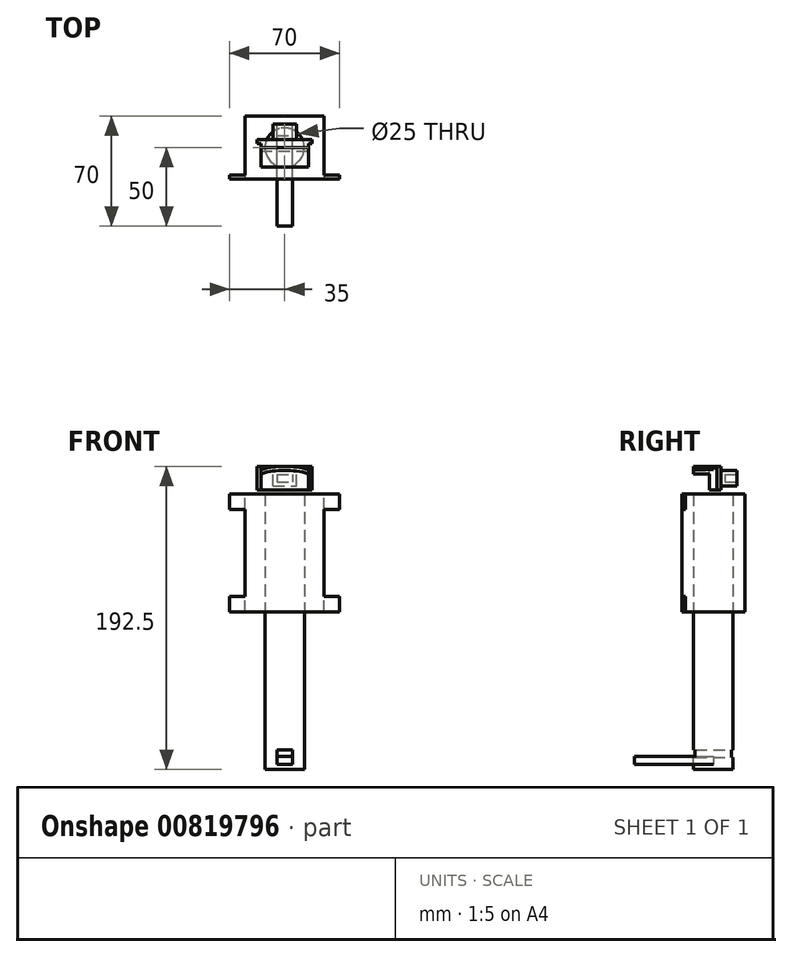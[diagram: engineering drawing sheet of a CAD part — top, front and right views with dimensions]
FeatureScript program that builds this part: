
annotation { "Feature Type Name" : "Feature", "Feature Type Description" : "" }
export const myFeature = defineFeature(function(context is Context, id is Id, definition is map)
    precondition{}
    {
        {
            var Q0;
            Q0=qCreatedBy(makeId("Front.planeOp"),FACE);
            var sketch = newSketch(context, id + "F0", { "sketchPlane" : qUnion([Q0])});
            skCircle(sketch, "E0", {"center": v(0, 0) * mm, "radius": 55 * mm});
            skSolve(sketch);
        }
        {
            var Q0;
            Q0=makeQuery(id+"F0.imprint","IMPRINT",FACE,{"disambiguationData":[TD([[makeQuery(id+"F0.imprint","IMPRINT",EDGE,{"derivedFrom":sQuery(id+"F0.wireOp",EDGE,"E0")}),1.0]])]});
            extrude(context, id + "F1", {"entities" : qUnion([Q0]), "depth" : 12.5 * mm, "offsetDistance" : 25 * mm});
        }
        {
            var Q0;
            Q0=makeQuery(id+"F1.opExtrude","CAP_FACE",FACE,{"disambiguationData":[OSD([sQuery(id+"F0.wireOp",EDGE,"E0")])],"isStart":false});
            shell(context, id + "F2", {"entities" : qUnion([Q0]), "thickness" : 2.5 * mm});
        }
        {
            var Q0;
            Q0=makeQuery(id+"F1.opExtrude","CAP_FACE",FACE,{"disambiguationData":[OSD([sQuery(id+"F0.wireOp",EDGE,"E0")])],"isStart":false});
            var sketch = newSketch(context, id + "F3", { "sketchPlane" : qUnion([Q0])});
            skLineSegment(sketch, "E1.bottom", {"start": v(-55, 55) * mm, "end": v(55, 55) * mm});
            skLineSegment(sketch, "E1.top", {"start": v(-55, -55) * mm, "end": v(55, -55) * mm});
            skLineSegment(sketch, "E1.left", {"start": v(-55, 55) * mm, "end": v(-55, -55) * mm});
            skLineSegment(sketch, "E1.right", {"start": v(55, 55) * mm, "end": v(55, -55) * mm});
            skPoint(sketch, "E1.middle", {"position": v(0, 0) * mm});
            skLineSegment(sketch, "E2.bottom", {"start": v(15, 55) * mm, "end": v(-15, 55) * mm});
            skLineSegment(sketch, "E2.top", {"start": v(15, 40) * mm, "end": v(-15, 40) * mm});
            skLineSegment(sketch, "E2.left", {"start": v(15, 55) * mm, "end": v(15, 40) * mm});
            skLineSegment(sketch, "E2.right", {"start": v(-15, 55) * mm, "end": v(-15, 40) * mm});
            skPoint(sketch, "E2.middle", {"position": v(0, 47.5) * mm});
            skPoint(sketch, "E2.middle.positionSnap0", {"position": v(0, 55) * mm});
            skPoint(sketch, "E2.centerSnap0", {"position": v(0, 55) * mm});
            skSolve(sketch);
        }
        {
            var Q0;
            {var subQ0=sQuery(id+"F3.wireOp",EDGE,"E2.top");Q0=makeQuery(id+"F3.imprint","IMPRINT",FACE,{"disambiguationData":[TD([[makeQuery(id+"F3.imprint","IMPRINT",EDGE,{"derivedFrom":subQ0}),1.0]])]});}
            var Q1;
            {var subQ0=sQuery(id+"F0.wireOp",EDGE,"E0");var subQ1=makeQuery(id+"F1.opExtrude","CAP_EDGE",EDGE,{"disambiguationData":[OSD([subQ0])],"isStart":false});var subQ2=makeQuery(id+"F3.imprint","INTERSECT",VERTEX,{"derivedFrom":[subQ1,sQuery(id+"F3.wireOp",EDGE,"E1.top")]});Q1=makeQuery(id+"F3.imprint","IMPRINT",FACE,{"disambiguationData":[TD([[makeQuery(id+"F3.imprint","IMPRINT",EDGE,{"disambiguationData":[TD([[subQ2,1.0]])],"derivedFrom":subQ1}),1.0]])]});}
            extrude(context, id + "F4", {"entities" : qUnion([Q0, Q1]), "operationType" : NewBodyOperationType.REMOVE, "oppositeDirection" : true, "depth" : 25 * mm, "offsetDistance" : 25 * mm});
        }
        {
            var Q0;
            Q0=makeQuery(id+"F4.boolean.opBoolean","COPY",FACE,{"derivedFrom":makeQuery(id+"F4.opExtrude","SWEPT_FACE",FACE,{"disambiguationData":[OSD([sQuery(id+"F3.wireOp",EDGE,"E2.top")])]})});
            var sketch = newSketch(context, id + "F5", { "sketchPlane" : qUnion([Q0])});
            skLineSegment(sketch, "E3.bottom", {"start": v(-15, 0) * mm, "end": v(15, 0) * mm});
            skLineSegment(sketch, "E3.top", {"start": v(-15, -5) * mm, "end": v(15, -5) * mm});
            skLineSegment(sketch, "E3.left", {"start": v(-15, 0) * mm, "end": v(-15, -5) * mm});
            skLineSegment(sketch, "E3.right", {"start": v(15, 0) * mm, "end": v(15, -5) * mm});
            skLineSegment(sketch, "E4.bottom", {"start": v(-15, -5) * mm, "end": v(-17.5, -5) * mm});
            skLineSegment(sketch, "E4.top", {"start": v(-15, -2.5) * mm, "end": v(-17.5, -2.5) * mm});
            skLineSegment(sketch, "E4.left", {"start": v(-15, -5) * mm, "end": v(-15, -2.5) * mm});
            skLineSegment(sketch, "E4.right", {"start": v(-17.5, -5) * mm, "end": v(-17.5, -2.5) * mm});
            skLineSegment(sketch, "E5.bottom", {"start": v(15, -5) * mm, "end": v(17.5, -5) * mm});
            skLineSegment(sketch, "E5.top", {"start": v(15, -2.5) * mm, "end": v(17.5, -2.5) * mm});
            skLineSegment(sketch, "E5.left", {"start": v(15, -5) * mm, "end": v(15, -2.5) * mm});
            skLineSegment(sketch, "E5.right", {"start": v(17.5, -5) * mm, "end": v(17.5, -2.5) * mm});
            skSolve(sketch);
        }
        {
            var Q0;
            Q0=makeQuery(id+"F5.imprint","IMPRINT",FACE,{"disambiguationData":[TD([[makeQuery(id+"F5.imprint","IMPRINT",EDGE,{"derivedFrom":sQuery(id+"F5.wireOp",EDGE,"E3.bottom")}),1.0]])]});
            var Q1;
            Q1=makeQuery(id+"F5.imprint","IMPRINT",FACE,{"disambiguationData":[TD([[makeQuery(id+"F5.imprint","IMPRINT",EDGE,{"derivedFrom":sQuery(id+"F5.wireOp",EDGE,"E5.bottom")}),1.0]])]});
            var Q2;
            Q2=makeQuery(id+"F5.imprint","IMPRINT",FACE,{"disambiguationData":[TD([[makeQuery(id+"F5.imprint","IMPRINT",EDGE,{"derivedFrom":sQuery(id+"F5.wireOp",EDGE,"E4.bottom")}),-1.0]])]});
            extrude(context, id + "F6", {"entities" : qUnion([Q0, Q1, Q2]), "operationType" : NewBodyOperationType.ADD, "oppositeDirection" : true, "depth" : 15 * mm, "offsetDistance" : 25 * mm});
        }
        {
            var Q0;
            Q0=makeQuery(id+"F6.opExtrude","SWEPT_FACE",FACE,{"disambiguationData":[OSD([sQuery(id+"F5.wireOp",EDGE,"E3.top"),sQuery(id+"F5.wireOp",EDGE,"E4.bottom"),sQuery(id+"F5.wireOp",EDGE,"E5.bottom")])]});
            var sketch = newSketch(context, id + "F7", { "sketchPlane" : qUnion([Q0])});
            skLineSegment(sketch, "E6.bottom", {"start": v(7.5, 42.5) * mm, "end": v(-7.5, 42.5) * mm});
            skLineSegment(sketch, "E6.top", {"start": v(7.5, 52.5) * mm, "end": v(-7.5, 52.5) * mm});
            skLineSegment(sketch, "E6.left", {"start": v(7.5, 42.5) * mm, "end": v(7.5, 52.5) * mm});
            skLineSegment(sketch, "E6.right", {"start": v(-7.5, 42.5) * mm, "end": v(-7.5, 52.5) * mm});
            skPoint(sketch, "E6.middle", {"position": v(0, 47.5) * mm});
            skSolve(sketch);
        }
        {
            var Q0;
            Q0=makeQuery(id+"F7.imprint","IMPRINT",FACE,{"disambiguationData":[TD([[makeQuery(id+"F7.imprint","IMPRINT",EDGE,{"derivedFrom":sQuery(id+"F7.wireOp",EDGE,"E6.bottom")}),-1.0]])]});
            extrude(context, id + "F8", {"entities" : qUnion([Q0]), "operationType" : NewBodyOperationType.ADD, "depth" : 10 * mm, "offsetDistance" : 25 * mm});
        }
        {
            var Q0;
            Q0=makeQuery(id+"F8.opExtrude","CAP_FACE",FACE,{"disambiguationData":[OSD([sQuery(id+"F7.wireOp",EDGE,"E6.bottom"),sQuery(id+"F7.wireOp",EDGE,"E6.top"),sQuery(id+"F7.wireOp",EDGE,"E6.left"),sQuery(id+"F7.wireOp",EDGE,"E6.right")])],"isStart":false});
            var sketch = newSketch(context, id + "F9", { "sketchPlane" : qUnion([Q0])});
            skLineSegment(sketch, "E7.bottom", {"start": v(5, 50) * mm, "end": v(-5, 50) * mm});
            skLineSegment(sketch, "E7.top", {"start": v(5, 45) * mm, "end": v(-5, 45) * mm});
            skLineSegment(sketch, "E7.left", {"start": v(5, 50) * mm, "end": v(5, 45) * mm});
            skLineSegment(sketch, "E7.right", {"start": v(-5, 50) * mm, "end": v(-5, 45) * mm});
            skPoint(sketch, "E7.middle", {"position": v(0, 47.5) * mm});
            skPoint(sketch, "E7.middle.positionSnap0", {"position": v(-7.5, 47.5) * mm});
            skPoint(sketch, "E7.centerSnap0", {"position": v(-7.5, 47.5) * mm});
            skSolve(sketch);
        }
        {
            var Q0;
            Q0=makeQuery(id+"F9.imprint","IMPRINT",FACE,{"disambiguationData":[TD([[makeQuery(id+"F9.imprint","IMPRINT",EDGE,{"derivedFrom":sQuery(id+"F9.wireOp",EDGE,"E7.bottom")}),1.0]])]});
            extrude(context, id + "F10", {"entities" : qUnion([Q0]), "operationType" : NewBodyOperationType.REMOVE, "oppositeDirection" : true, "depth" : 7.5 * mm, "offsetDistance" : 25 * mm});
        }
        {
            var Q0;
            Q0=qCreatedBy(makeId("Front.planeOp"),FACE);
            var sketch = newSketch(context, id + "F11", { "sketchPlane" : qUnion([Q0])});
            skLineSegment(sketch, "E8.bottom", {"start": v(25, -37.5) * mm, "end": v(-25, -37.5) * mm});
            skLineSegment(sketch, "E8.top", {"start": v(25, 37.5) * mm, "end": v(-25, 37.5) * mm});
            skLineSegment(sketch, "E8.left", {"start": v(25, -37.5) * mm, "end": v(25, 37.5) * mm});
            skLineSegment(sketch, "E8.right", {"start": v(-25, -37.5) * mm, "end": v(-25, 37.5) * mm});
            skPoint(sketch, "E8.middle", {"position": v(0, 0) * mm});
            skSolve(sketch);
        }
        {
            var Q0;
            Q0=makeQuery(id+"F11.imprint","IMPRINT",FACE,{"disambiguationData":[TD([[makeQuery(id+"F11.imprint","IMPRINT",EDGE,{"derivedFrom":sQuery(id+"F11.wireOp",EDGE,"E8.bottom")}),-1.0]])]});
            extrude(context, id + "F12", {"entities" : qUnion([Q0]), "endBound" : BoundingType.SYMMETRIC, "depth" : 40 * mm, "offsetDistance" : 25 * mm});
        }
        {
            var Q0;
            Q0=makeQuery(id+"F12.opExtrude","SWEPT_FACE",FACE,{"disambiguationData":[OSD([sQuery(id+"F11.wireOp",EDGE,"E8.bottom")])]});
            var sketch = newSketch(context, id + "F13", { "sketchPlane" : qUnion([Q0])});
            skCircle(sketch, "E9", {"center": v(0, 0) * mm, "radius": 12.5 * mm});
            skSolve(sketch);
        }
        {
            var Q0;
            Q0=makeQuery(id+"F13.imprint","IMPRINT",FACE,{"disambiguationData":[TD([[makeQuery(id+"F13.imprint","IMPRINT",EDGE,{"derivedFrom":sQuery(id+"F13.wireOp",EDGE,"E9")}),1.0]])]});
            extrude(context, id + "F14", {"entities" : qUnion([Q0]), "operationType" : NewBodyOperationType.REMOVE, "oppositeDirection" : true, "depth" : 75 * mm, "offsetDistance" : 25 * mm});
        }
        {
            var Q0;
            Q0=makeQuery(id+"F12.opExtrude","CAP_FACE",FACE,{"disambiguationData":[OSD([sQuery(id+"F11.wireOp",EDGE,"E8.bottom"),sQuery(id+"F11.wireOp",EDGE,"E8.top"),sQuery(id+"F11.wireOp",EDGE,"E8.left"),sQuery(id+"F11.wireOp",EDGE,"E8.right")])],"isStart":false});
            var sketch = newSketch(context, id + "F15", { "sketchPlane" : qUnion([Q0])});
            skLineSegment(sketch, "E10.bottom", {"start": v(25, 37.5) * mm, "end": v(35, 37.5) * mm});
            skLineSegment(sketch, "E10.top", {"start": v(25, 27.5) * mm, "end": v(35, 27.5) * mm});
            skLineSegment(sketch, "E10.left", {"start": v(25, 37.5) * mm, "end": v(25, 27.5) * mm});
            skLineSegment(sketch, "E10.right", {"start": v(35, 37.5) * mm, "end": v(35, 27.5) * mm});
            skLineSegment(sketch, "E11.bottom", {"start": v(-25, 37.5) * mm, "end": v(-35, 37.5) * mm});
            skLineSegment(sketch, "E11.top", {"start": v(-25, 27.5) * mm, "end": v(-35, 27.5) * mm});
            skLineSegment(sketch, "E11.left", {"start": v(-25, 37.5) * mm, "end": v(-25, 27.5) * mm});
            skLineSegment(sketch, "E11.right", {"start": v(-35, 37.5) * mm, "end": v(-35, 27.5) * mm});
            skLineSegment(sketch, "E12.bottom", {"start": v(-25, -37.5) * mm, "end": v(-35, -37.5) * mm});
            skLineSegment(sketch, "E12.top", {"start": v(-25, -27.5) * mm, "end": v(-35, -27.5) * mm});
            skLineSegment(sketch, "E12.left", {"start": v(-25, -37.5) * mm, "end": v(-25, -27.5) * mm});
            skLineSegment(sketch, "E12.right", {"start": v(-35, -37.5) * mm, "end": v(-35, -27.5) * mm});
            skLineSegment(sketch, "E13.bottom", {"start": v(25, -37.5) * mm, "end": v(35, -37.5) * mm});
            skLineSegment(sketch, "E13.top", {"start": v(25, -27.5) * mm, "end": v(35, -27.5) * mm});
            skLineSegment(sketch, "E13.left", {"start": v(25, -37.5) * mm, "end": v(25, -27.5) * mm});
            skLineSegment(sketch, "E13.right", {"start": v(35, -37.5) * mm, "end": v(35, -27.5) * mm});
            skSolve(sketch);
        }
        {
            var Q0;
            Q0=makeQuery(id+"F15.imprint","IMPRINT",FACE,{"disambiguationData":[TD([[makeQuery(id+"F15.imprint","IMPRINT",EDGE,{"derivedFrom":sQuery(id+"F15.wireOp",EDGE,"E11.bottom")}),1.0]])]});
            var Q1;
            Q1=makeQuery(id+"F15.imprint","IMPRINT",FACE,{"disambiguationData":[TD([[makeQuery(id+"F15.imprint","IMPRINT",EDGE,{"derivedFrom":sQuery(id+"F15.wireOp",EDGE,"E10.bottom")}),-1.0]])]});
            var Q2;
            Q2=makeQuery(id+"F15.imprint","IMPRINT",FACE,{"disambiguationData":[TD([[makeQuery(id+"F15.imprint","IMPRINT",EDGE,{"derivedFrom":sQuery(id+"F15.wireOp",EDGE,"E12.bottom")}),-1.0]])]});
            var Q3;
            Q3=makeQuery(id+"F15.imprint","IMPRINT",FACE,{"disambiguationData":[TD([[makeQuery(id+"F15.imprint","IMPRINT",EDGE,{"derivedFrom":sQuery(id+"F15.wireOp",EDGE,"E13.bottom")}),1.0]])]});
            extrude(context, id + "F16", {"entities" : qUnion([Q0, Q1, Q2, Q3]), "operationType" : NewBodyOperationType.ADD, "oppositeDirection" : true, "depth" : 2.5 * mm, "offsetDistance" : 25 * mm});
        }
        {
            var Q0;
            Q0=makeQuery(id+"F12.opExtrude","CAP_FACE",FACE,{"disambiguationData":[OSD([sQuery(id+"F11.wireOp",EDGE,"E8.bottom"),sQuery(id+"F11.wireOp",EDGE,"E8.top"),sQuery(id+"F11.wireOp",EDGE,"E8.left"),sQuery(id+"F11.wireOp",EDGE,"E8.right")])],"isStart":true});
            var sketch = newSketch(context, id + "F17", { "sketchPlane" : qUnion([Q0])});
            skLineSegment(sketch, "E14.bottom", {"start": v(5, -130) * mm, "end": v(-5, -130) * mm});
            skLineSegment(sketch, "E14.top", {"start": v(5, -125) * mm, "end": v(-5, -125) * mm});
            skLineSegment(sketch, "E14.left", {"start": v(5, -130) * mm, "end": v(5, -125) * mm});
            skLineSegment(sketch, "E14.right", {"start": v(-5, -130) * mm, "end": v(-5, -125) * mm});
            skPoint(sketch, "E14.middle", {"position": v(0, -127.5) * mm});
            skSolve(sketch);
        }
        {
            var Q0;
            Q0 = qSketchRegion(id + "F13", true);
            extrude(context, id + "F18", {"entities" : qUnion([Q0]), "depth" : 100 * mm, "offsetDistance" : 25 * mm});
        }
        {
            var Q0;
            Q0=makeQuery(id+"F17.imprint","IMPRINT",FACE,{"disambiguationData":[TD([[makeQuery(id+"F17.imprint","IMPRINT",EDGE,{"derivedFrom":sQuery(id+"F17.wireOp",EDGE,"E14.bottom")}),-1.0]])]});
            extrude(context, id + "F19", {"entities" : qUnion([Q0]), "operationType" : NewBodyOperationType.REMOVE, "oppositeDirection" : true, "depth" : 40 * mm, "offsetDistance" : 25 * mm});
        }
        {
            var Q0;
            Q0=qCreatedBy(makeId("Front.planeOp"),FACE);
            var sketch = newSketch(context, id + "F20", { "sketchPlane" : qUnion([Q0])});
            skLineSegment(sketch, "E15.bottom", {"start": v(-5, -129.29) * mm, "end": v(5, -129.29) * mm});
            skLineSegment(sketch, "E15.top", {"start": v(-5, -134.29) * mm, "end": v(5, -134.29) * mm});
            skLineSegment(sketch, "E15.left", {"start": v(-5, -129.29) * mm, "end": v(-5, -134.29) * mm});
            skLineSegment(sketch, "E15.right", {"start": v(5, -129.29) * mm, "end": v(5, -134.29) * mm});
            skPoint(sketch, "E15.middle", {"position": v(0, -131.79) * mm});
            skSolve(sketch);
        }
        {
            var Q0;
            Q0=makeQuery(id+"F20.imprint","IMPRINT",FACE,{"disambiguationData":[TD([[makeQuery(id+"F20.imprint","IMPRINT",EDGE,{"derivedFrom":sQuery(id+"F20.wireOp",EDGE,"E15.bottom")}),-1.0]])]});
            extrude(context, id + "F21", {"entities" : qUnion([Q0]), "depth" : 50 * mm, "offsetDistance" : 25 * mm});
        }
    });
